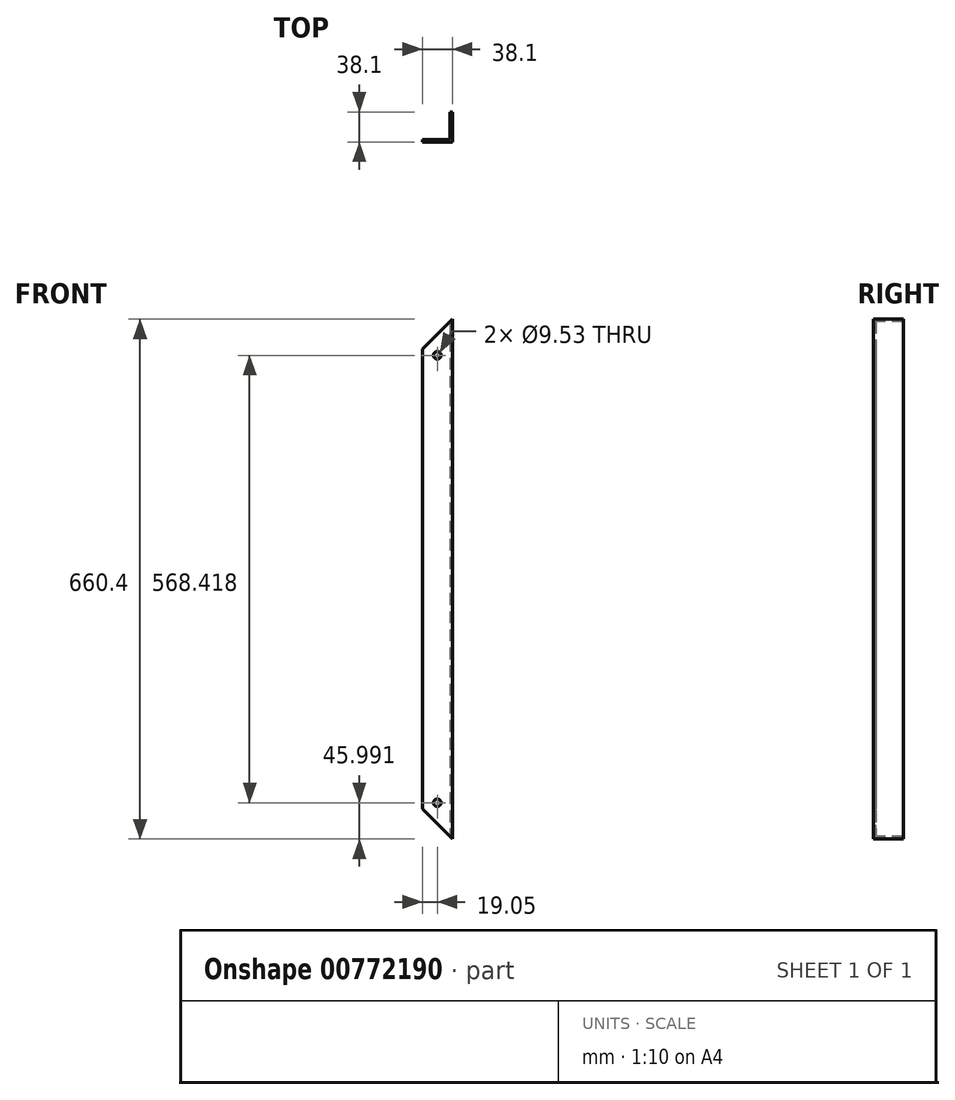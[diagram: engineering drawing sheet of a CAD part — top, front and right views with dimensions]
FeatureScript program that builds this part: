
annotation { "Feature Type Name" : "Feature", "Feature Type Description" : "" }
export const myFeature = defineFeature(function(context is Context, id is Id, definition is map)
    precondition{}
    {
        {
            var Q0;
            Q0=qCreatedBy(makeId("Top.planeOp"),FACE);
            var sketch = newSketch(context, id + "F0", { "sketchPlane" : qUnion([Q0])});
            skLineSegment(sketch, "E0", {"start": v(0, 0) * mm, "end": v(38.1, 0) * mm});
            skLineSegment(sketch, "E1", {"start": v(38.1, 0) * mm, "end": v(38.1, 38.1) * mm});
            skLineSegment(sketch, "E2", {"start": v(38.1, 38.1) * mm, "end": v(34.92, 38.1) * mm});
            skLineSegment(sketch, "E3", {"start": v(34.92, 38.1) * mm, "end": v(34.93, 3.18) * mm});
            skLineSegment(sketch, "E4", {"start": v(34.93, 3.18) * mm, "end": v(0, 3.18) * mm});
            skLineSegment(sketch, "E5", {"start": v(0, 3.17) * mm, "end": v(0, 0) * mm});
            skSolve(sketch);
        }
        {
            var Q0;
            Q0=makeQuery(id+"F0.imprint","IMPRINT",FACE,{"disambiguationData":[TD([[makeQuery(id+"F0.imprint","IMPRINT",EDGE,{"derivedFrom":sQuery(id+"F0.wireOp",EDGE,"E0")}),1.0]])]});
            extrude(context, id + "F1", {"entities" : qUnion([Q0]), "depth" : 660.4 * mm, "offsetDistance" : 25.4 * mm});
        }
        {
            var Q0;
            Q0=makeQuery(id+"F1.opExtrude","SWEPT_FACE",FACE,{"disambiguationData":[OSD([sQuery(id+"F0.wireOp",EDGE,"E0")])]});
            var sketch = newSketch(context, id + "F2", { "sketchPlane" : qUnion([Q0])});
            skLineSegment(sketch, "E6", {"start": v(38.1, 660.4) * mm, "end": v(0, 622.3) * mm});
            skLineSegment(sketch, "E7", {"start": v(38.1, 0) * mm, "end": v(0, 38.1) * mm});
            skSolve(sketch);
        }
        {
            var Q0;
            {var subQ0=sQuery(id+"F2.wireOp",EDGE,"E6");Q0=makeQuery(id+"F2.imprint","IMPRINT",FACE,{"disambiguationData":[TD([[makeQuery(id+"F2.imprint","IMPRINT",EDGE,{"derivedFrom":subQ0}),-1.0]])]});}
            var Q1;
            {var subQ0=sQuery(id+"F2.wireOp",EDGE,"E7");Q1=makeQuery(id+"F2.imprint","IMPRINT",FACE,{"disambiguationData":[TD([[makeQuery(id+"F2.imprint","IMPRINT",EDGE,{"derivedFrom":subQ0}),1.0]])]});}
            extrude(context, id + "F3", {"entities" : qUnion([Q0, Q1]), "operationType" : NewBodyOperationType.REMOVE, "endBound" : BoundingType.THROUGH_ALL, "oppositeDirection" : true, "depth" : 25.4 * mm, "offsetDistance" : 25.4 * mm});
        }
        {
            var Q0;
            Q0=makeQuery(id+"F1.opExtrude","SWEPT_FACE",FACE,{"disambiguationData":[OSD([sQuery(id+"F0.wireOp",EDGE,"E0")])]});
            var sketch = newSketch(context, id + "F4", { "sketchPlane" : qUnion([Q0])});
            skCircle(sketch, "E8", {"center": v(19.05, 614.4) * mm, "radius": 4.76 * mm});
            skCircle(sketch, "E9", {"center": v(19.05, 46) * mm, "radius": 4.76 * mm});
            skSolve(sketch);
        }
        {
            var Q0;
            Q0=makeQuery(id+"F4.imprint","IMPRINT",FACE,{"disambiguationData":[TD([[makeQuery(id+"F4.imprint","IMPRINT",EDGE,{"derivedFrom":sQuery(id+"F4.wireOp",EDGE,"E9")}),1.0]])]});
            var Q1;
            Q1=makeQuery(id+"F4.imprint","IMPRINT",FACE,{"disambiguationData":[TD([[makeQuery(id+"F4.imprint","IMPRINT",EDGE,{"derivedFrom":sQuery(id+"F4.wireOp",EDGE,"E8")}),1.0]])]});
            extrude(context, id + "F5", {"entities" : qUnion([Q0, Q1]), "operationType" : NewBodyOperationType.REMOVE, "endBound" : BoundingType.THROUGH_ALL, "oppositeDirection" : true, "depth" : 25.4 * mm, "offsetDistance" : 25.4 * mm});
        }
    });
